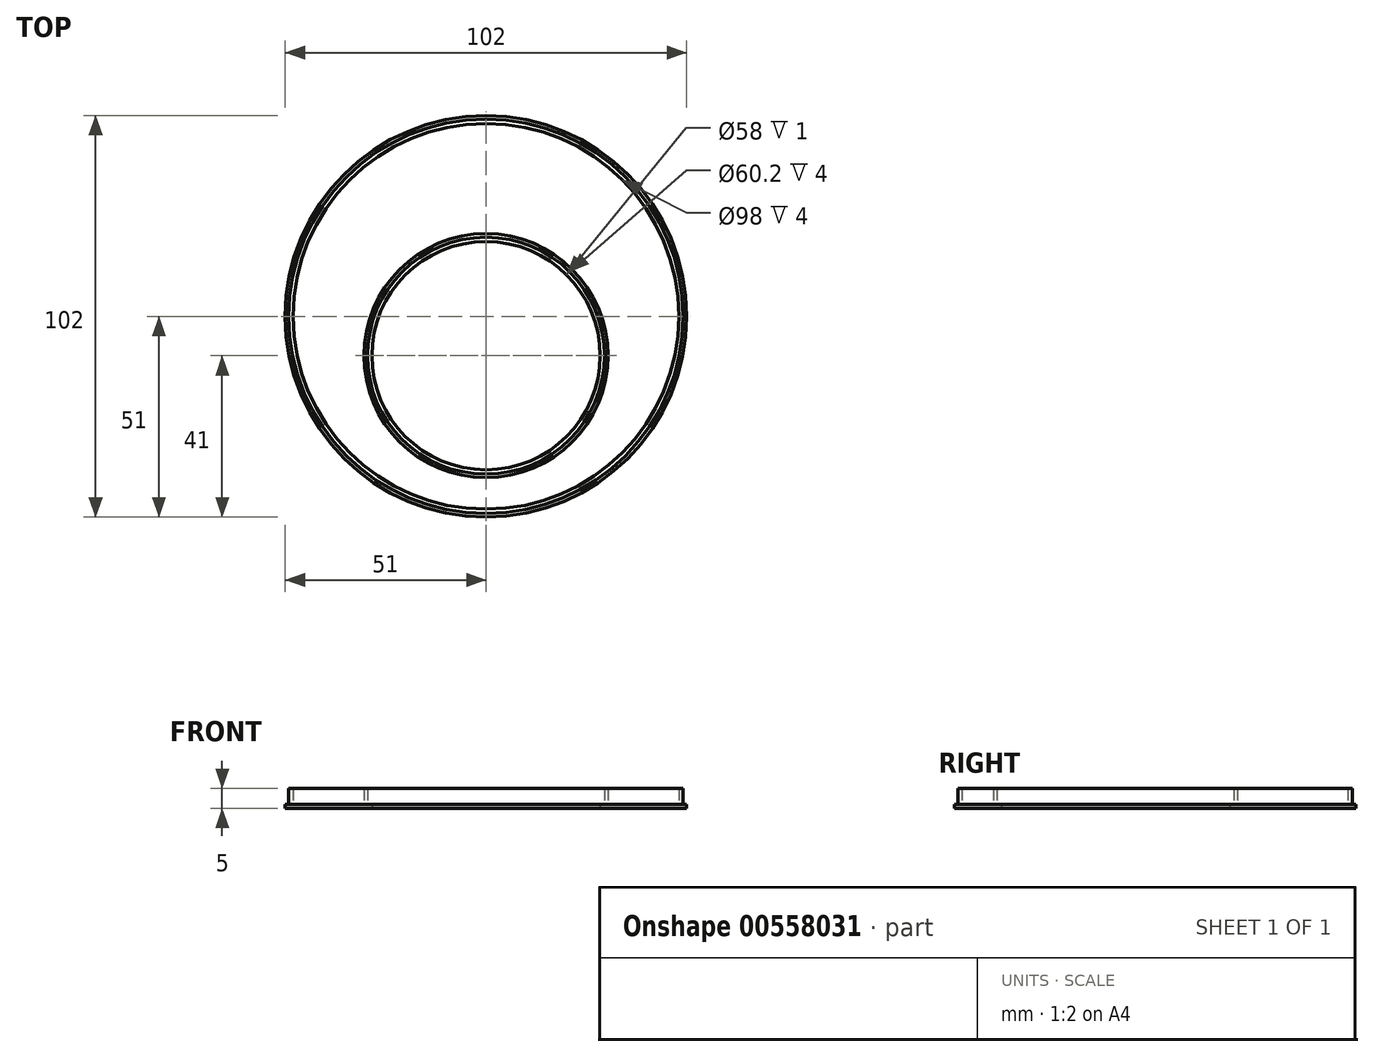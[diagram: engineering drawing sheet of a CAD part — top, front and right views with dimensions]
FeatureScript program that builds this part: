
annotation { "Feature Type Name" : "Feature", "Feature Type Description" : "" }
export const myFeature = defineFeature(function(context is Context, id is Id, definition is map)
    precondition{}
    {
        {
            var Q0;
            Q0=qCreatedBy(makeId("Top.planeOp"),FACE);
            var sketch = newSketch(context, id + "F0", { "sketchPlane" : qUnion([Q0])});
            skCircle(sketch, "E0", {"center": v(0, 0) * mm, "radius": 50.1 * mm});
            skLineSegment(sketch, "E1", {"start": v(0, 64.4) * mm, "end": v(0, -71.07) * mm, "construction": true});
            skCircle(sketch, "E2", {"center": v(0, -10) * mm, "radius": 31 * mm});
            skCircle(sketch, "E3", {"center": v(0, 0) * mm, "radius": 51 * mm});
            skCircle(sketch, "E4", {"center": v(0, -10) * mm, "radius": 30.1 * mm});
            skLineSegment(sketch, "E5", {"start": v(-62.85, -10) * mm, "end": v(56.48, -10) * mm, "construction": true});
            skCircle(sketch, "E6", {"center": v(0, -10) * mm, "radius": 29 * mm});
            skCircle(sketch, "E7", {"center": v(0, 0) * mm, "radius": 49 * mm});
            skSolve(sketch);
        }
        {
            var Q0;
            Q0=makeQuery(id+"F0.imprint","IMPRINT",FACE,{"disambiguationData":[TD([[makeQuery(id+"F0.imprint","IMPRINT",EDGE,{"derivedFrom":sQuery(id+"F0.wireOp",EDGE,"E0")}),-1.0]])]});
            var Q1;
            Q1=makeQuery(id+"F0.imprint","IMPRINT",FACE,{"disambiguationData":[TD([[makeQuery(id+"F0.imprint","IMPRINT",EDGE,{"derivedFrom":sQuery(id+"F0.wireOp",EDGE,"E4")}),1.0]])]});
            var Q2;
            Q2=makeQuery(id+"F0.imprint","IMPRINT",FACE,{"disambiguationData":[TD([[makeQuery(id+"F0.imprint","IMPRINT",EDGE,{"derivedFrom":sQuery(id+"F0.wireOp",EDGE,"E2")}),-1.0]])]});
            extrude(context, id + "F1", {"entities" : qUnion([Q0, Q1, Q2]), "depth" : 1 * mm, "offsetDistance" : 25 * mm});
        }
        {
            var Q0;
            Q0=makeQuery(id+"F0.imprint","IMPRINT",FACE,{"disambiguationData":[TD([[makeQuery(id+"F0.imprint","IMPRINT",EDGE,{"derivedFrom":sQuery(id+"F0.wireOp",EDGE,"E0")}),1.0]])]});
            var Q1;
            Q1=makeQuery(id+"F0.imprint","IMPRINT",FACE,{"disambiguationData":[TD([[makeQuery(id+"F0.imprint","IMPRINT",EDGE,{"derivedFrom":sQuery(id+"F0.wireOp",EDGE,"E2")}),1.0]])]});
            extrude(context, id + "F2", {"entities" : qUnion([Q0, Q1]), "operationType" : NewBodyOperationType.ADD, "depth" : 5 * mm, "offsetDistance" : 25 * mm});
        }
    });
